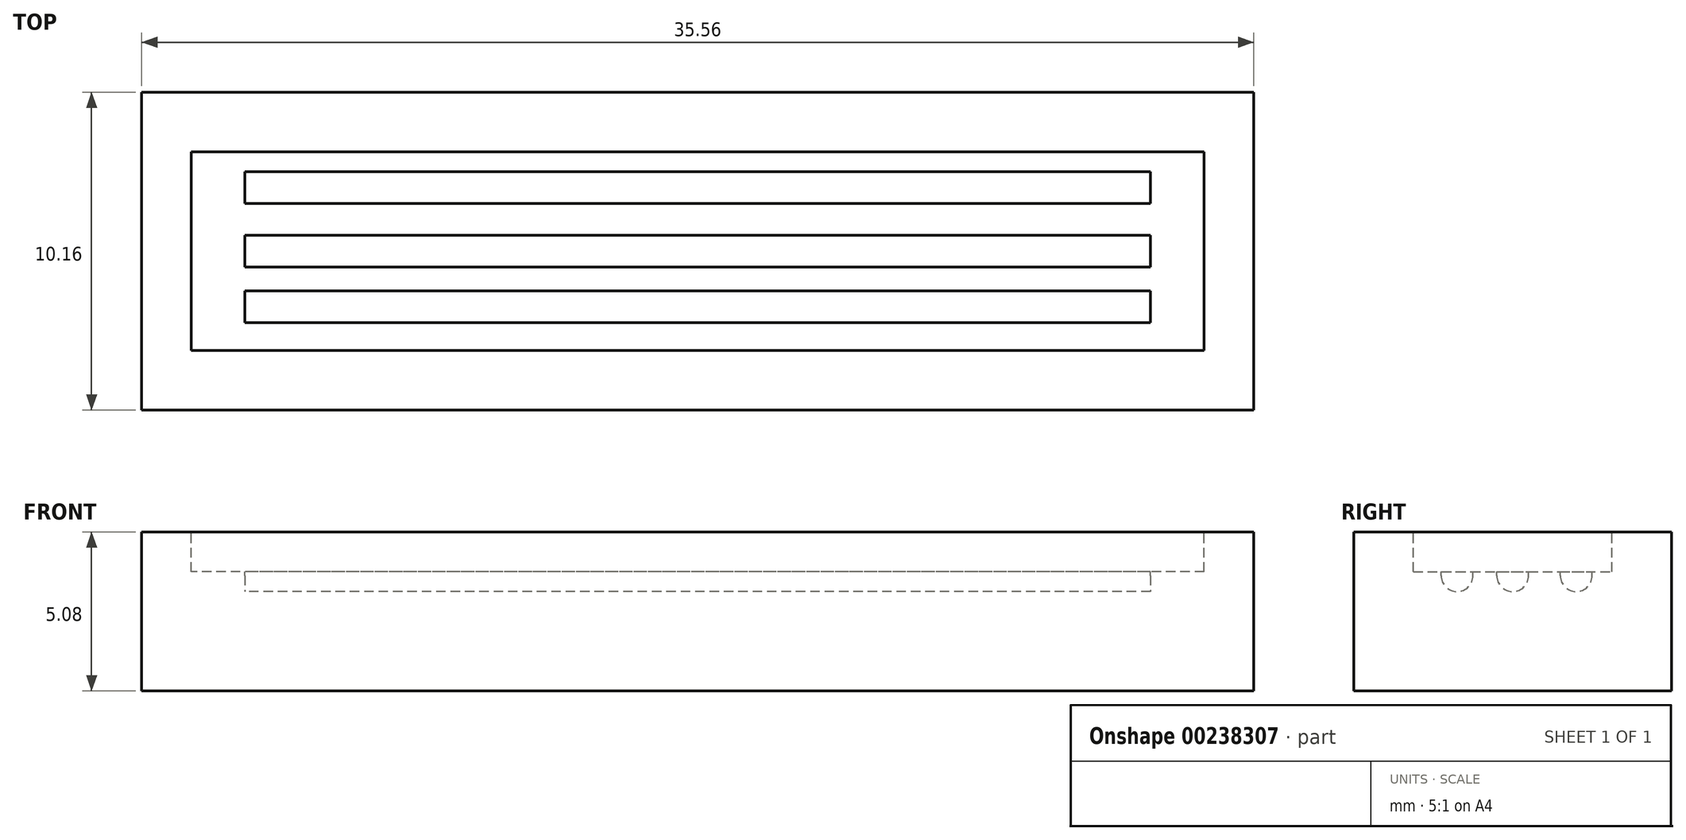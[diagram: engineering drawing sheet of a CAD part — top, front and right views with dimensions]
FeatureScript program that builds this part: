
annotation { "Feature Type Name" : "Feature", "Feature Type Description" : "" }
export const myFeature = defineFeature(function(context is Context, id is Id, definition is map)
    precondition{}
    {
        {
            var Q0;
            Q0=qCreatedBy(makeId("Top.planeOp"),FACE);
            var sketch = newSketch(context, id + "F0", { "sketchPlane" : qUnion([Q0])});
            skLineSegment(sketch, "E0.bottom", {"start": v(17.78, -5.08) * mm, "end": v(-17.78, -5.08) * mm});
            skLineSegment(sketch, "E0.top", {"start": v(17.78, 5.08) * mm, "end": v(-17.78, 5.08) * mm});
            skLineSegment(sketch, "E0.left", {"start": v(17.78, -5.08) * mm, "end": v(17.78, 5.08) * mm});
            skLineSegment(sketch, "E0.right", {"start": v(-17.78, -5.08) * mm, "end": v(-17.78, 5.08) * mm});
            skPoint(sketch, "E0.middle", {"position": v(0, 0) * mm});
            skSolve(sketch);
        }
        {
            var Q0;
            Q0=makeQuery(id+"F0.imprint","IMPRINT",FACE,{"disambiguationData":[TD([[makeQuery(id+"F0.imprint","IMPRINT",EDGE,{"derivedFrom":sQuery(id+"F0.wireOp",EDGE,"E0.bottom")}),-1.0]])]});
            extrude(context, id + "F1", {"entities" : qUnion([Q0]), "depth" : 5.08 * mm});
        }
        {
            var Q0;
            Q0=makeQuery(id+"F1.opExtrude","CAP_FACE",FACE,{"disambiguationData":[OSD([sQuery(id+"F0.wireOp",EDGE,"E0.bottom"),sQuery(id+"F0.wireOp",EDGE,"E0.top"),sQuery(id+"F0.wireOp",EDGE,"E0.left"),sQuery(id+"F0.wireOp",EDGE,"E0.right")])],"isStart":false});
            var sketch = newSketch(context, id + "F2", { "sketchPlane" : qUnion([Q0])});
            skLineSegment(sketch, "E1.bottom", {"start": v(16.2, -3.18) * mm, "end": v(-16.2, -3.18) * mm});
            skLineSegment(sketch, "E1.top", {"start": v(16.2, 3.18) * mm, "end": v(-16.2, 3.18) * mm});
            skLineSegment(sketch, "E1.left", {"start": v(16.2, -3.18) * mm, "end": v(16.2, 3.17) * mm});
            skLineSegment(sketch, "E1.right", {"start": v(-16.2, -3.18) * mm, "end": v(-16.2, 3.17) * mm});
            skPoint(sketch, "E1.middle", {"position": v(0, 0) * mm});
            skSolve(sketch);
        }
        {
            var Q0;
            Q0=qSketchRegion(id+"F2",true);
            extrude(context, id + "F3", {"entities" : qUnion([Q0]), "operationType" : NewBodyOperationType.REMOVE, "oppositeDirection" : true, "depth" : 1.27 * mm});
        }
        {
            var Q0;
            Q0=makeQuery(id+"F3.boolean.opBoolean","COPY",FACE,{"derivedFrom":makeQuery(id+"F3.opExtrude","CAP_FACE",FACE,{"disambiguationData":[OSD([sQuery(id+"F2.wireOp",EDGE,"E1.bottom"),sQuery(id+"F2.wireOp",EDGE,"E1.top"),sQuery(id+"F2.wireOp",EDGE,"E1.left"),sQuery(id+"F2.wireOp",EDGE,"E1.right")])],"isStart":false})});
            var sketch = newSketch(context, id + "F4", { "sketchPlane" : qUnion([Q0])});
            skLineSegment(sketch, "E2.bottom", {"start": v(14.48, -0.5) * mm, "end": v(-14.48, -0.5) * mm});
            skLineSegment(sketch, "E2.top", {"start": v(14.48, 0.5) * mm, "end": v(-14.48, 0.5) * mm});
            skLineSegment(sketch, "E2.left", {"start": v(14.48, -0.5) * mm, "end": v(14.48, 0.5) * mm});
            skLineSegment(sketch, "E2.right", {"start": v(-14.48, -0.5) * mm, "end": v(-14.48, 0.5) * mm});
            skPoint(sketch, "E2.middle", {"position": v(0, 0) * mm});
            skLineSegment(sketch, "E3.0.1.0", {"start": v(14.48, 2.54) * mm, "end": v(-14.48, 2.54) * mm});
            skLineSegment(sketch, "E3.0.1.1", {"start": v(14.48, 1.52) * mm, "end": v(-14.48, 1.52) * mm});
            skLineSegment(sketch, "E3.0.1.2", {"start": v(-14.48, 1.52) * mm, "end": v(-14.48, 2.54) * mm});
            skLineSegment(sketch, "E3.0.1.3", {"start": v(14.48, 1.52) * mm, "end": v(14.48, 2.54) * mm});
            skLineSegment(sketch, "E3.direction1", {"start": v(-14.48, 0.5) * mm, "end": v(10.92, 0.5) * mm, "construction": true});
            skLineSegment(sketch, "E3.direction2", {"start": v(-14.48, 0.5) * mm, "end": v(-14.48, 2.54) * mm, "construction": true});
            skLineSegment(sketch, "E4.0.1.0", {"start": v(14.48, -2.29) * mm, "end": v(-14.48, -2.29) * mm});
            skLineSegment(sketch, "E4.0.1.1", {"start": v(-14.48, -2.29) * mm, "end": v(-14.48, -1.27) * mm});
            skLineSegment(sketch, "E4.0.1.2", {"start": v(14.48, -1.27) * mm, "end": v(-14.48, -1.27) * mm});
            skLineSegment(sketch, "E4.0.1.3", {"start": v(14.48, -2.29) * mm, "end": v(14.48, -1.27) * mm});
            skLineSegment(sketch, "E4.direction1", {"start": v(-14.48, -0.5) * mm, "end": v(10.92, -0.5) * mm, "construction": true});
            skLineSegment(sketch, "E4.direction2", {"start": v(-14.48, -0.5) * mm, "end": v(-14.48, -2.29) * mm, "construction": true});
            skSolve(sketch);
        }
        {
            var Q0;
            Q0 = qSketchRegion(id + "F4", true);
            extrude(context, id + "F5", {"entities" : qUnion([Q0]), "operationType" : NewBodyOperationType.REMOVE, "oppositeDirection" : true, "depth" : 0.64 * mm});
        }
        {
            var Q0;
            Q0=makeQuery(id+"F5.boolean.opBoolean","COPY",EDGE,{"derivedFrom":makeQuery(id+"F5.opExtrude","CAP_EDGE",EDGE,{"disambiguationData":[OSD([sQuery(id+"F4.wireOp",EDGE,"E2.top")])],"isStart":false})});
            var Q1;
            Q1=makeQuery(id+"F5.boolean.opBoolean","COPY",EDGE,{"derivedFrom":makeQuery(id+"F5.opExtrude","CAP_EDGE",EDGE,{"disambiguationData":[OSD([sQuery(id+"F4.wireOp",EDGE,"E2.bottom")])],"isStart":false})});
            var Q2;
            Q2=makeQuery(id+"F5.boolean.opBoolean","COPY",EDGE,{"derivedFrom":makeQuery(id+"F5.opExtrude","CAP_EDGE",EDGE,{"disambiguationData":[OSD([sQuery(id+"F4.wireOp",EDGE,"E3.0.1.0")])],"isStart":false})});
            var Q3;
            Q3=makeQuery(id+"F5.boolean.opBoolean","COPY",EDGE,{"derivedFrom":makeQuery(id+"F5.opExtrude","CAP_EDGE",EDGE,{"disambiguationData":[OSD([sQuery(id+"F4.wireOp",EDGE,"E4.0.1.2")])],"isStart":false})});
            var Q4;
            Q4=makeQuery(id+"F5.boolean.opBoolean","COPY",EDGE,{"derivedFrom":makeQuery(id+"F5.opExtrude","CAP_EDGE",EDGE,{"disambiguationData":[OSD([sQuery(id+"F4.wireOp",EDGE,"E3.0.1.1")])],"isStart":false})});
            var Q5;
            Q5=makeQuery(id+"F5.boolean.opBoolean","COPY",EDGE,{"derivedFrom":makeQuery(id+"F5.opExtrude","CAP_EDGE",EDGE,{"disambiguationData":[OSD([sQuery(id+"F4.wireOp",EDGE,"E4.0.1.0")])],"isStart":false})});
            fillet(context, id + "F6", {"entities" : qUnion([Q0, Q1, Q2, Q3, Q4, Q5]), "radius" : 0.5 * mm, "tangentPropagation" : true, "allowEdgeOverflow" : false});
        }
    });
